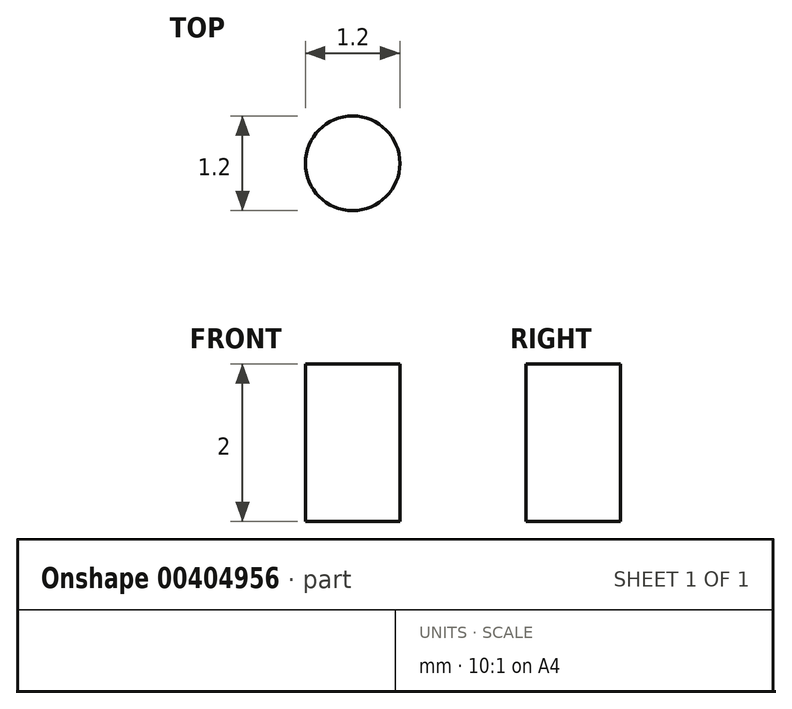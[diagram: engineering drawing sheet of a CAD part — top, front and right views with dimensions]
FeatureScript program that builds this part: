
annotation { "Feature Type Name" : "Feature", "Feature Type Description" : "" }
export const myFeature = defineFeature(function(context is Context, id is Id, definition is map)
    precondition{}
    {
        {
            var Q0;
            Q0=qCreatedBy(makeId("Top.planeOp"),FACE);
            var sketch = newSketch(context, id + "F0", { "sketchPlane" : qUnion([Q0])});
            skCircle(sketch, "E0", {"center": v(0, 0) * mm, "radius": 0.6 * mm});
            skSolve(sketch);
        }
        {
            var Q0;
            Q0 = qSketchRegion(id + "F0", true);
            extrude(context, id + "F1", {"entities" : qUnion([Q0]), "depth" : 2 * mm});
        }
    });
